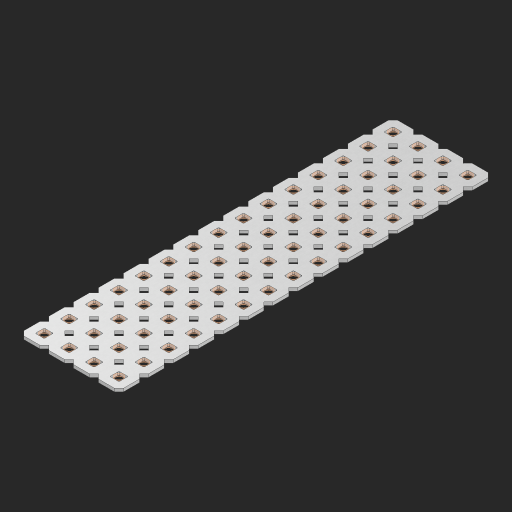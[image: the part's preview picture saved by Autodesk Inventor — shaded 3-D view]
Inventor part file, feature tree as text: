
AUTODESK INVENTOR PART (.ipt)
format: ipt  version: 2023 (Build 270158000, 158)  size: 980,992 bytes
history: native  units: in
note: dims shown in document units (in); Inventor stores cm internally (conversion verified against a paired STEP export)
features: other x61, extrude x59, sketch x2, pattern_linear x1
ambient origin geometry x8: Origin, YZ Plane, XZ Plane, XY Plane, X Axis, Y Axis, Z Axis, Center Point
bodies: Solid1 (feature_tree), Body (feature_tree)
feature tree (123):
  pattern_linear  "Rectangular Pattern1"  Spacing1=0.09in  [1 undecoded]
  sketch  "Sketch1"  dims[d1=0.5in]
  sketch  "Sketch2"  dims[d2=0.182in d3=0.09in d4=0.09in d5=0.09in d6=0.09in d7=0.09in d8=0.09in d9=0.09in d10=0.09in d11=0.02in d13=0.0in d14=0.172in d15=0.0625in d16=0.0in d19=0.5in d22=0.5in]
  other  "Srf1"
  other  "Srf126"
  other  "Srf127"
  other  "Srf128"
  other  "Srf129"
  other  "Srf130"
  other  "Srf131"
  other  "Srf250"
  other  "Srf251"
  other  "Srf252"
  other  "Srf253"
  other  "Srf254"
  other  "Srf255"
  other  "Srf256"
  other  "Srf257"
  other  "Srf268"
  other  "Srf269"
  other  "Srf270"
  other  "Srf271"
  other  "Srf272"
  other  "Srf273"
  other  "Srf274"
  other  "Srf275"
  other  "Srf276"
  other  "Srf277"
  other  "Srf278"
  other  "Srf279"
  other  "Srf280"
  other  "Srf281"
  other  "Srf282"
  other  "Srf293"
  other  "Srf294"
  other  "Srf295"
  other  "Srf296"
  other  "Srf297"
  other  "Srf298"
  other  "Srf299"
  other  "Srf300"
  other  "Srf301"
  other  "Srf302"
  other  "Srf303"
  other  "Srf304"
  other  "Srf305"
  other  "Srf306"
  other  "Srf307"
  other  "Srf318"
  other  "Srf319"
  other  "Srf320"
  other  "Srf321"
  other  "Srf322"
  other  "Srf323"
  other  "Srf324"
  other  "Srf325"
  other  "Srf326"
  other  "Srf327"
  other  "Srf328"
  other  "Srf329"
  other  "Srf330"
  other  "Srf331"
  other  "Srf332"
  other  "Circle"
  extrude  "ExtrusionSrf126"  Depth=0.09in
  extrude  "ExtrusionSrf127"  Depth=0.09in
  extrude  "ExtrusionSrf128"  Depth=0.09in
  extrude  "ExtrusionSrf129"  Depth=0.09in
  extrude  "ExtrusionSrf130"  Depth=0.09in
  extrude  "ExtrusionSrf131"  Depth=0.09in
  extrude  "ExtrusionSrf250"  Depth=0.09in
  extrude  "ExtrusionSrf251"  Depth=0.02in
  extrude  "ExtrusionSrf252"  TaperAngle=0.0deg  [1 undecoded]
  extrude  "ExtrusionSrf253"  Depth=0.5in
  extrude  "ExtrusionSrf254"  Depth=0.0625in TaperAngle=0.0deg
  extrude  "ExtrusionSrf255"  Depth=0.5in
  extrude  "ExtrusionSrf256"  Depth=0.5in
  extrude  "ExtrusionSrf257"  [1 undecoded]
  extrude  "ExtrusionSrf268"  [1 undecoded]
  extrude  "ExtrusionSrf269"  [1 undecoded]
  extrude  "ExtrusionSrf270"  [1 undecoded]
  extrude  "ExtrusionSrf271"  [1 undecoded]
  extrude  "ExtrusionSrf272"  [1 undecoded]
  extrude  "ExtrusionSrf273"  [1 undecoded]
  extrude  "ExtrusionSrf274"  [1 undecoded]
  extrude  "ExtrusionSrf275"  [1 undecoded]
  extrude  "ExtrusionSrf276"  [1 undecoded]
  extrude  "ExtrusionSrf277"  [1 undecoded]
  extrude  "ExtrusionSrf278"  [1 undecoded]
  extrude  "ExtrusionSrf279"  [1 undecoded]
  extrude  "ExtrusionSrf280"  [1 undecoded]
  extrude  "ExtrusionSrf281"  [1 undecoded]
  extrude  "ExtrusionSrf282"  [1 undecoded]
  extrude  "ExtrusionSrf293"  [1 undecoded]
  extrude  "ExtrusionSrf294"  [1 undecoded]
  extrude  "ExtrusionSrf295"  [1 undecoded]
  extrude  "ExtrusionSrf296"  [1 undecoded]
  extrude  "ExtrusionSrf297"  [1 undecoded]
  extrude  "ExtrusionSrf298"  [1 undecoded]
  extrude  "ExtrusionSrf299"  [1 undecoded]
  extrude  "ExtrusionSrf300"  [1 undecoded]
  extrude  "ExtrusionSrf301"  [1 undecoded]
  extrude  "ExtrusionSrf302"  [1 undecoded]
  extrude  "ExtrusionSrf303"  [1 undecoded]
  extrude  "ExtrusionSrf304"  [1 undecoded]
  extrude  "ExtrusionSrf305"  [1 undecoded]
  extrude  "ExtrusionSrf306"  [1 undecoded]
  extrude  "ExtrusionSrf307"  [1 undecoded]
  extrude  "ExtrusionSrf318"  [1 undecoded]
  extrude  "ExtrusionSrf319"  [1 undecoded]
  extrude  "ExtrusionSrf320"  [1 undecoded]
  extrude  "ExtrusionSrf321"  [1 undecoded]
  extrude  "ExtrusionSrf322"  [1 undecoded]
  extrude  "ExtrusionSrf323"  [1 undecoded]
  extrude  "ExtrusionSrf324"  [1 undecoded]
  extrude  "ExtrusionSrf325"  [1 undecoded]
  extrude  "ExtrusionSrf326"  [1 undecoded]
  extrude  "ExtrusionSrf327"  [1 undecoded]
  extrude  "ExtrusionSrf328"  [1 undecoded]
  extrude  "ExtrusionSrf329"  [1 undecoded]
  extrude  "ExtrusionSrf330"  [1 undecoded]
  extrude  "ExtrusionSrf331"  [1 undecoded]
  extrude  "ExtrusionSrf332"  [1 undecoded]
note: 48 required parameter values undecoded (feature->parameter linkage not recoverable at this tier; creation-order binding heuristic only, values carry confidence <= 0.55)
